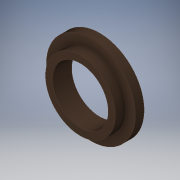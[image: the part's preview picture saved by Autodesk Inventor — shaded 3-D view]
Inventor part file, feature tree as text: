
AUTODESK INVENTOR PART (.ipt)
format: ipt  version: 2018 (Build 220112000, 112)  size: 117,248 bytes
history: native  units: mm
features: revolve x1, sketch x1
ambient origin geometry x8: Origin, YZ Plane, XZ Plane, XY Plane, X Axis, Y Axis, Z Axis, Center Point
bodies: Solid1 (feature_tree)
feature tree (2):
  revolve  "Revolution1"  [1 undecoded]
  sketch  "Sketch1"  dims[d0=16.0mm d1=11.0mm d2=9.5mm d3=5.0mm d4=4.0mm d5=90.0deg]
note: 1 required parameter value undecoded (feature->parameter linkage not recoverable at this tier; creation-order binding heuristic only, values carry confidence <= 0.55)
